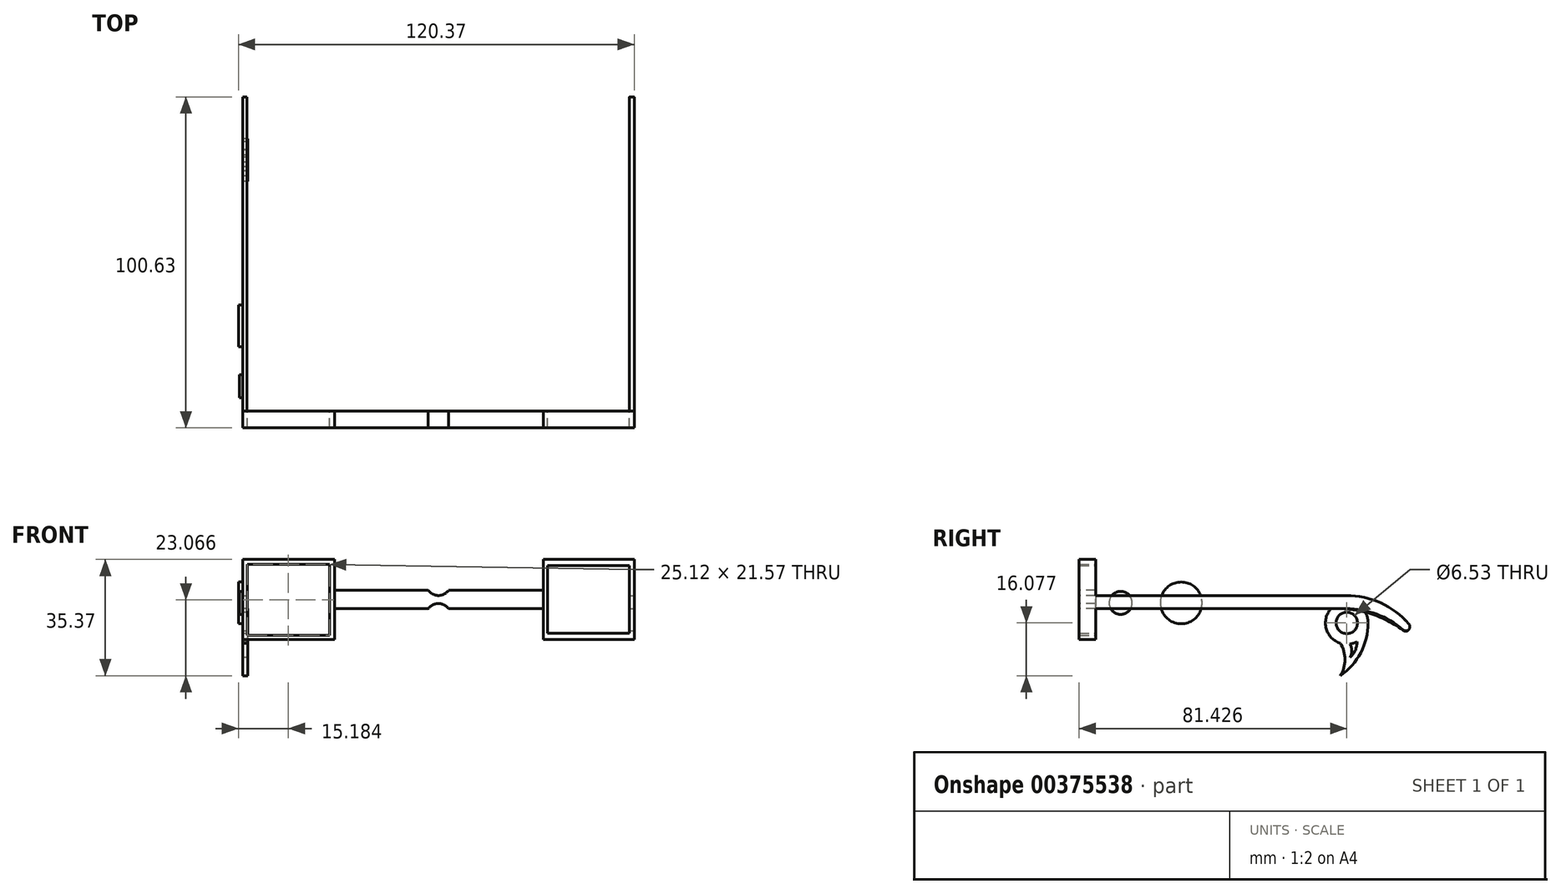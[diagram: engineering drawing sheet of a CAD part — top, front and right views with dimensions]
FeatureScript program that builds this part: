
annotation { "Feature Type Name" : "Feature", "Feature Type Description" : "" }
export const myFeature = defineFeature(function(context is Context, id is Id, definition is map)
    precondition{}
    {
        {
            var Q0;
            Q0=qCreatedBy(makeId("Front.planeOp"),FACE);
            var sketch = newSketch(context, id + "F0", { "sketchPlane" : qUnion([Q0])});
            skLineSegment(sketch, "E0", {"start": v(26.39, 5.58) * mm, "end": v(26.39, 0) * mm});
            skLineSegment(sketch, "E1", {"start": v(-37.11, 0) * mm, "end": v(-37.11, 5.58) * mm});
            skLineSegment(sketch, "E2", {"start": v(-37.11, 5.58) * mm, "end": v(-37.11, 14.97) * mm});
            skLineSegment(sketch, "E3", {"start": v(-37.11, 14.97) * mm, "end": v(-65.11, 14.97) * mm});
            skLineSegment(sketch, "E4", {"start": v(-65.11, 14.97) * mm, "end": v(-65.11, -9.39) * mm});
            skLineSegment(sketch, "E5", {"start": v(-65.11, -9.39) * mm, "end": v(-37.11, -9.39) * mm});
            skLineSegment(sketch, "E6", {"start": v(-37.11, -9.39) * mm, "end": v(-37.11, 0) * mm});
            skLineSegment(sketch, "E7", {"start": v(26.39, 5.58) * mm, "end": v(26.39, 14.97) * mm});
            skLineSegment(sketch, "E8", {"start": v(26.39, 14.97) * mm, "end": v(54, 14.97) * mm});
            skLineSegment(sketch, "E9", {"start": v(54, 14.97) * mm, "end": v(54, -9.39) * mm});
            skLineSegment(sketch, "E10", {"start": v(54, -9.39) * mm, "end": v(26.39, -9.39) * mm});
            skLineSegment(sketch, "E11", {"start": v(26.39, -9.39) * mm, "end": v(26.39, 0) * mm});
            skLineSegment(sketch, "E12.bottom", {"start": v(-63.76, 13.45) * mm, "end": v(-38.64, 13.45) * mm});
            skLineSegment(sketch, "E12.top", {"start": v(-63.76, -8.12) * mm, "end": v(-38.64, -8.12) * mm});
            skLineSegment(sketch, "E12.left", {"start": v(-63.76, 13.45) * mm, "end": v(-63.76, -8.12) * mm});
            skLineSegment(sketch, "E12.right", {"start": v(-38.64, 13.45) * mm, "end": v(-38.64, -8.12) * mm});
            skLineSegment(sketch, "E13.bottom", {"start": v(27.66, 13.06) * mm, "end": v(52.52, 13.06) * mm});
            skLineSegment(sketch, "E13.top", {"start": v(27.66, -7.46) * mm, "end": v(52.52, -7.46) * mm});
            skLineSegment(sketch, "E13.left", {"start": v(27.66, 13.06) * mm, "end": v(27.66, -7.46) * mm});
            skLineSegment(sketch, "E13.right", {"start": v(52.52, 13.06) * mm, "end": v(52.52, -7.46) * mm});
            skLineSegment(sketch, "E14", {"start": v(-37.11, 5.58) * mm, "end": v(26.39, 5.58) * mm});
            skLineSegment(sketch, "E15", {"start": v(26.39, 0) * mm, "end": v(-37.11, 0) * mm});
            skSolve(sketch);
        }
        {
            var Q0;
            Q0=makeQuery(id+"F0.imprint","IMPRINT",FACE,{"disambiguationData":[TD([[makeQuery(id+"F0.imprint","IMPRINT",EDGE,{"derivedFrom":sQuery(id+"F0.wireOp",EDGE,"E0")}),1.0]])]});
            var Q1;
            Q1=makeQuery(id+"F0.imprint","IMPRINT",FACE,{"disambiguationData":[TD([[makeQuery(id+"F0.imprint","IMPRINT",EDGE,{"derivedFrom":sQuery(id+"F0.wireOp",EDGE,"E1")}),1.0]])]});
            extrude(context, id + "F1", {"entities" : qUnion([Q0, Q1]), "depth" : 5.08 * mm});
        }
        {
            var Q0;
            Q0=makeQuery(id+"F0.imprint","IMPRINT",FACE,{"disambiguationData":[TD([[makeQuery(id+"F0.imprint","IMPRINT",EDGE,{"derivedFrom":sQuery(id+"F0.wireOp",EDGE,"E12.bottom")}),-1.0]])]});
            var Q1;
            Q1=makeQuery(id+"F0.imprint","IMPRINT",FACE,{"disambiguationData":[TD([[makeQuery(id+"F0.imprint","IMPRINT",EDGE,{"derivedFrom":sQuery(id+"F0.wireOp",EDGE,"E13.bottom")}),-1.0]])]});
            extrude(context, id + "F2", {"entities" : qUnion([Q0, Q1]), "operationType" : NewBodyOperationType.REMOVE, "depth" : 5.08 * mm});
        }
        {
            var Q0;
            Q0=makeQuery(id+"F0.imprint","IMPRINT",FACE,{"disambiguationData":[TD([[makeQuery(id+"F0.imprint","IMPRINT",EDGE,{"derivedFrom":sQuery(id+"F0.wireOp",EDGE,"E0")}),-1.0]])]});
            extrude(context, id + "F3", {"entities" : qUnion([Q0]), "depth" : 5.08 * mm});
        }
        {
            var Q0;
            Q0=makeQuery(id+"F1.opExtrude","SWEPT_FACE",FACE,{"disambiguationData":[OSD([sQuery(id+"F0.wireOp",EDGE,"E4")])]});
            var sketch = newSketch(context, id + "F4", { "sketchPlane" : qUnion([Q0])});
            skLineSegment(sketch, "E16", {"start": v(0, 3.78) * mm, "end": v(-76.2, 3.78) * mm});
            skArc(sketch, "E17", {"start": v(-76.2, 3.78) * mm, "mid": v(-86.6, 1.55) * mm, "end": v(-95.18, -4.74) * mm});
            skLineSegment(sketch, "E18", {"start": v(0, 0) * mm, "end": v(-73.66, 0) * mm});
            skArc(sketch, "E19", {"start": v(-73.66, 0) * mm, "mid": v(-84.1, -1.7) * mm, "end": v(-93.47, -6.6) * mm});
            skPoint(sketch, "E20.visualSharp", {"position": v(-100.24, -13.43) * mm});
            skArc(sketch, "E20.filletArc", {"start": v(-95.18, -4.74) * mm, "mid": v(-95.17, -6.45) * mm, "end": v(-93.47, -6.6) * mm});
            skSolve(sketch);
        }
        {
            var Q0;
            {var subQ1=sQuery(id+"F4.wireOp",EDGE,"E16");Q0=makeQuery(id+"F4.imprint","IMPRINT",FACE,{"disambiguationData":[TD([[makeQuery(id+"F4.imprint","IMPRINT",EDGE,{"derivedFrom":subQ1}),1.0]])]});}
            extrude(context, id + "F5", {"entities" : qUnion([Q0]), "operationType" : NewBodyOperationType.ADD, "oppositeDirection" : true, "depth" : 1.27 * mm});
        }
        {
            var Q0;
            Q0=makeQuery(id+"F1.opExtrude","SWEPT_FACE",FACE,{"disambiguationData":[OSD([sQuery(id+"F0.wireOp",EDGE,"E9")])]});
            var sketch = newSketch(context, id + "F6", { "sketchPlane" : qUnion([Q0])});
            skPoint(sketch, "E21.visualSharp", {"position": v(84.8, -2.01) * mm});
            skPoint(sketch, "E22.visualSharp", {"position": v(83.57, -2.01) * mm});
            skLineSegment(sketch, "E23", {"start": v(0, 4.02) * mm, "end": v(76.2, 4.02) * mm});
            skLineSegment(sketch, "E24", {"start": v(0, 0) * mm, "end": v(76.2, 0) * mm});
            skArc(sketch, "E25", {"start": v(95.24, -4.66) * mm, "mid": v(86.66, 1.75) * mm, "end": v(76.2, 4.02) * mm});
            skArc(sketch, "E26", {"start": v(93.45, -6.44) * mm, "mid": v(85.4, -1.66) * mm, "end": v(76.2, 0) * mm});
            skArc(sketch, "E27", {"start": v(93.45, -6.44) * mm, "mid": v(95.18, -6.38) * mm, "end": v(95.24, -4.66) * mm});
            skSolve(sketch);
        }
        {
            var Q0;
            {var subQ1=sQuery(id+"F6.wireOp",EDGE,"E23");Q0=makeQuery(id+"F6.imprint","IMPRINT",FACE,{"disambiguationData":[TD([[makeQuery(id+"F6.imprint","IMPRINT",EDGE,{"derivedFrom":subQ1}),-1.0]])]});}
            extrude(context, id + "F7", {"entities" : qUnion([Q0]), "operationType" : NewBodyOperationType.ADD, "oppositeDirection" : true, "depth" : 1.52 * mm});
        }
        {
            var Q0;
            Q0=makeQuery(id+"F3.opExtrude","CAP_FACE",FACE,{"disambiguationData":[OSD([sQuery(id+"F0.wireOp",EDGE,"E0"),sQuery(id+"F0.wireOp",EDGE,"E1"),sQuery(id+"F0.wireOp",EDGE,"E14"),sQuery(id+"F0.wireOp",EDGE,"E15")])],"isStart":false});
            var sketch = newSketch(context, id + "F8", { "sketchPlane" : qUnion([Q0])});
            skArc(sketch, "E28", {"start": v(-8.65, 5.58) * mm, "mid": v(-5.56, 4) * mm, "end": v(-2.48, 5.58) * mm});
            skArc(sketch, "E29", {"start": v(-2.48, 0) * mm, "mid": v(-5.56, 1.58) * mm, "end": v(-8.65, 0) * mm});
            skSolve(sketch);
        }
        {
            var Q0;
            {var subQ0=sQuery(id+"F8.wireOp",EDGE,"E28");Q0=makeQuery(id+"F8.imprint","IMPRINT",FACE,{"disambiguationData":[TD([[makeQuery(id+"F8.imprint","IMPRINT",EDGE,{"derivedFrom":subQ0}),1.0]])]});}
            var Q1;
            {var subQ0=sQuery(id+"F8.wireOp",EDGE,"E29");Q1=makeQuery(id+"F8.imprint","IMPRINT",FACE,{"disambiguationData":[TD([[makeQuery(id+"F8.imprint","IMPRINT",EDGE,{"derivedFrom":subQ0}),1.0]])]});}
            extrude(context, id + "F9", {"entities" : qUnion([Q0, Q1]), "operationType" : NewBodyOperationType.REMOVE, "oppositeDirection" : true, "depth" : 25.4 * mm});
        }
        {
            var Q0;
            {var subQ0=sQuery(id+"F0.wireOp",EDGE,"E4");Q0=makeQuery(id+"F5.boolean.opBoolean","MERGE",FACE,{"derivedFrom":[makeQuery(id+"F1.opExtrude","SWEPT_FACE",FACE,{"disambiguationData":[OSD([subQ0])]}),makeQuery(id+"F5.opExtrude","CAP_FACE",FACE,{"disambiguationData":[OSD([subQ0,sQuery(id+"F4.wireOp",EDGE,"E16"),sQuery(id+"F4.wireOp",EDGE,"E17"),sQuery(id+"F4.wireOp",EDGE,"E18"),sQuery(id+"F4.wireOp",EDGE,"E19"),sQuery(id+"F4.wireOp",EDGE,"E20.filletArc")])],"isStart":true})]});}
            var sketch = newSketch(context, id + "F10", { "sketchPlane" : qUnion([Q0])});
            skCircle(sketch, "E30", {"center": v(-76.35, -4.32) * mm, "radius": 6.48 * mm});
            skArc(sketch, "E31", {"start": v(-74.38, -10.5) * mm, "mid": v(-75.78, -15.45) * mm, "end": v(-74.38, -20.4) * mm});
            skArc(sketch, "E32", {"start": v(-82.83, -4.32) * mm, "mid": v(-80.59, -13.4) * mm, "end": v(-74.38, -20.4) * mm});
            skCircle(sketch, "E33", {"center": v(-76.35, -4.32) * mm, "radius": 3.26 * mm});
            skArc(sketch, "E34", {"start": v(-79.45, -10.01) * mm, "mid": v(-78.91, -12.68) * mm, "end": v(-77.3, -14.87) * mm});
            skArc(sketch, "E35", {"start": v(-77.3, -10.73) * mm, "mid": v(-77.89, -12.8) * mm, "end": v(-77.3, -14.87) * mm});
            skSolve(sketch);
        }
        {
            var Q0;
            {var subQ3=sQuery(id+"F10.wireOp",EDGE,"E30");var subQ6=makeQuery(id+"F10.imprint","INTERSECT",VERTEX,{"derivedFrom":[subQ3,sQuery(id+"F10.wireOp",EDGE,"E32")]});Q0=makeQuery(id+"F10.imprint","IMPRINT",FACE,{"disambiguationData":[TD([[makeQuery(id+"F10.imprint","IMPRINT",EDGE,{"disambiguationData":[TD([[subQ6,1.0]])],"derivedFrom":subQ3}),1.0]])]});}
            var Q1;
            {var subQ0=sQuery(id+"F10.wireOp",EDGE,"E31");Q1=makeQuery(id+"F10.imprint","IMPRINT",FACE,{"disambiguationData":[TD([[makeQuery(id+"F10.imprint","IMPRINT",EDGE,{"derivedFrom":subQ0}),-1.0]])]});}
            extrude(context, id + "F11", {"entities" : qUnion([Q0, Q1]), "oppositeDirection" : true, "depth" : 1.52 * mm});
        }
        {
            var Q0;
            Q0=makeQuery(id+"F10.imprint","IMPRINT",FACE,{"disambiguationData":[TD([[makeQuery(id+"F10.imprint","IMPRINT",EDGE,{"derivedFrom":sQuery(id+"F10.wireOp",EDGE,"E33")}),1.0]])]});
            var Q1;
            {var subQ0=sQuery(id+"F10.wireOp",EDGE,"E34");Q1=makeQuery(id+"F10.imprint","IMPRINT",FACE,{"disambiguationData":[TD([[makeQuery(id+"F10.imprint","IMPRINT",EDGE,{"derivedFrom":subQ0}),1.0]])]});}
            extrude(context, id + "F12", {"entities" : qUnion([Q0, Q1]), "operationType" : NewBodyOperationType.REMOVE, "oppositeDirection" : true, "depth" : 25.4 * mm});
        }
        {
            var Q0;
            {var subQ0=sQuery(id+"F0.wireOp",EDGE,"E4");Q0=makeQuery(id+"F5.boolean.opBoolean","MERGE",FACE,{"derivedFrom":[makeQuery(id+"F1.opExtrude","SWEPT_FACE",FACE,{"disambiguationData":[OSD([subQ0])]}),makeQuery(id+"F5.opExtrude","CAP_FACE",FACE,{"disambiguationData":[OSD([subQ0,sQuery(id+"F4.wireOp",EDGE,"E16"),sQuery(id+"F4.wireOp",EDGE,"E17"),sQuery(id+"F4.wireOp",EDGE,"E18"),sQuery(id+"F4.wireOp",EDGE,"E19"),sQuery(id+"F4.wireOp",EDGE,"E20.filletArc")])],"isStart":true})]});}
            var sketch = newSketch(context, id + "F13", { "sketchPlane" : qUnion([Q0])});
            skCircle(sketch, "E36", {"center": v(-7.56, 1.76) * mm, "radius": 3.5 * mm});
            skCircle(sketch, "E37", {"center": v(-25.98, 1.76) * mm, "radius": 6.35 * mm});
            skSolve(sketch);
        }
        {
            var Q0;
            {var subQ0=sQuery(id+"F13.wireOp",EDGE,"E36");var subQ1=makeQuery(id+"F5.opExtrude","CAP_EDGE",EDGE,{"disambiguationData":[OSD([sQuery(id+"F4.wireOp",EDGE,"E18")])],"isStart":true});var subQ2=makeQuery(id+"F13.imprint","INTERSECT",VERTEX,{"disambiguationData":[OD(0.0)],"derivedFrom":[subQ1,subQ0]});Q0=makeQuery(id+"F13.imprint","IMPRINT",FACE,{"disambiguationData":[TD([[makeQuery(id+"F13.imprint","IMPRINT",EDGE,{"disambiguationData":[TD([[subQ2,-1.0]])],"derivedFrom":subQ0}),1.0]])]});}
            var Q1;
            {var subQ0=sQuery(id+"F13.wireOp",EDGE,"E36");var subQ1=makeQuery(id+"F5.opExtrude","CAP_EDGE",EDGE,{"disambiguationData":[OSD([sQuery(id+"F4.wireOp",EDGE,"E16")])],"isStart":true});var subQ2=makeQuery(id+"F13.imprint","INTERSECT",VERTEX,{"disambiguationData":[OD(0.0)],"derivedFrom":[subQ1,subQ0]});Q1=makeQuery(id+"F13.imprint","IMPRINT",FACE,{"disambiguationData":[TD([[makeQuery(id+"F13.imprint","IMPRINT",EDGE,{"disambiguationData":[TD([[subQ2,-1.0]])],"derivedFrom":subQ0}),1.0]])]});}
            var Q2;
            {var subQ0=sQuery(id+"F13.wireOp",EDGE,"E36");var subQ1=makeQuery(id+"F5.opExtrude","CAP_EDGE",EDGE,{"disambiguationData":[OSD([sQuery(id+"F4.wireOp",EDGE,"E16")])],"isStart":true});var subQ2=makeQuery(id+"F13.imprint","INTERSECT",VERTEX,{"disambiguationData":[OD(0.0)],"derivedFrom":[subQ1,subQ0]});Q2=makeQuery(id+"F13.imprint","IMPRINT",FACE,{"disambiguationData":[TD([[makeQuery(id+"F13.imprint","IMPRINT",EDGE,{"disambiguationData":[TD([[subQ2,1.0]])],"derivedFrom":subQ0}),1.0]])]});}
            extrude(context, id + "F14", {"entities" : qUnion([Q0, Q1, Q2]), "operationType" : NewBodyOperationType.ADD, "depth" : 1.02 * mm});
        }
        {
            var Q0;
            {var subQ0=sQuery(id+"F13.wireOp",EDGE,"E37");var subQ1=makeQuery(id+"F5.opExtrude","CAP_EDGE",EDGE,{"disambiguationData":[OSD([sQuery(id+"F4.wireOp",EDGE,"E18")])],"isStart":true});var subQ2=makeQuery(id+"F13.imprint","INTERSECT",VERTEX,{"disambiguationData":[OD(0.0)],"derivedFrom":[subQ1,subQ0]});Q0=makeQuery(id+"F13.imprint","IMPRINT",FACE,{"disambiguationData":[TD([[makeQuery(id+"F13.imprint","IMPRINT",EDGE,{"disambiguationData":[TD([[subQ2,-1.0]])],"derivedFrom":subQ0}),1.0]])]});}
            var Q1;
            {var subQ0=sQuery(id+"F13.wireOp",EDGE,"E37");var subQ1=makeQuery(id+"F5.opExtrude","CAP_EDGE",EDGE,{"disambiguationData":[OSD([sQuery(id+"F4.wireOp",EDGE,"E16")])],"isStart":true});var subQ2=makeQuery(id+"F13.imprint","INTERSECT",VERTEX,{"disambiguationData":[OD(0.0)],"derivedFrom":[subQ1,subQ0]});Q1=makeQuery(id+"F13.imprint","IMPRINT",FACE,{"disambiguationData":[TD([[makeQuery(id+"F13.imprint","IMPRINT",EDGE,{"disambiguationData":[TD([[subQ2,-1.0]])],"derivedFrom":subQ0}),1.0]])]});}
            var Q2;
            {var subQ0=sQuery(id+"F13.wireOp",EDGE,"E37");var subQ1=makeQuery(id+"F5.opExtrude","CAP_EDGE",EDGE,{"disambiguationData":[OSD([sQuery(id+"F4.wireOp",EDGE,"E16")])],"isStart":true});var subQ2=makeQuery(id+"F13.imprint","INTERSECT",VERTEX,{"disambiguationData":[OD(0.0)],"derivedFrom":[subQ1,subQ0]});Q2=makeQuery(id+"F13.imprint","IMPRINT",FACE,{"disambiguationData":[TD([[makeQuery(id+"F13.imprint","IMPRINT",EDGE,{"disambiguationData":[TD([[subQ2,1.0]])],"derivedFrom":subQ0}),1.0]])]});}
            extrude(context, id + "F15", {"entities" : qUnion([Q0, Q1, Q2]), "operationType" : NewBodyOperationType.ADD, "depth" : 1.27 * mm});
        }
    });
